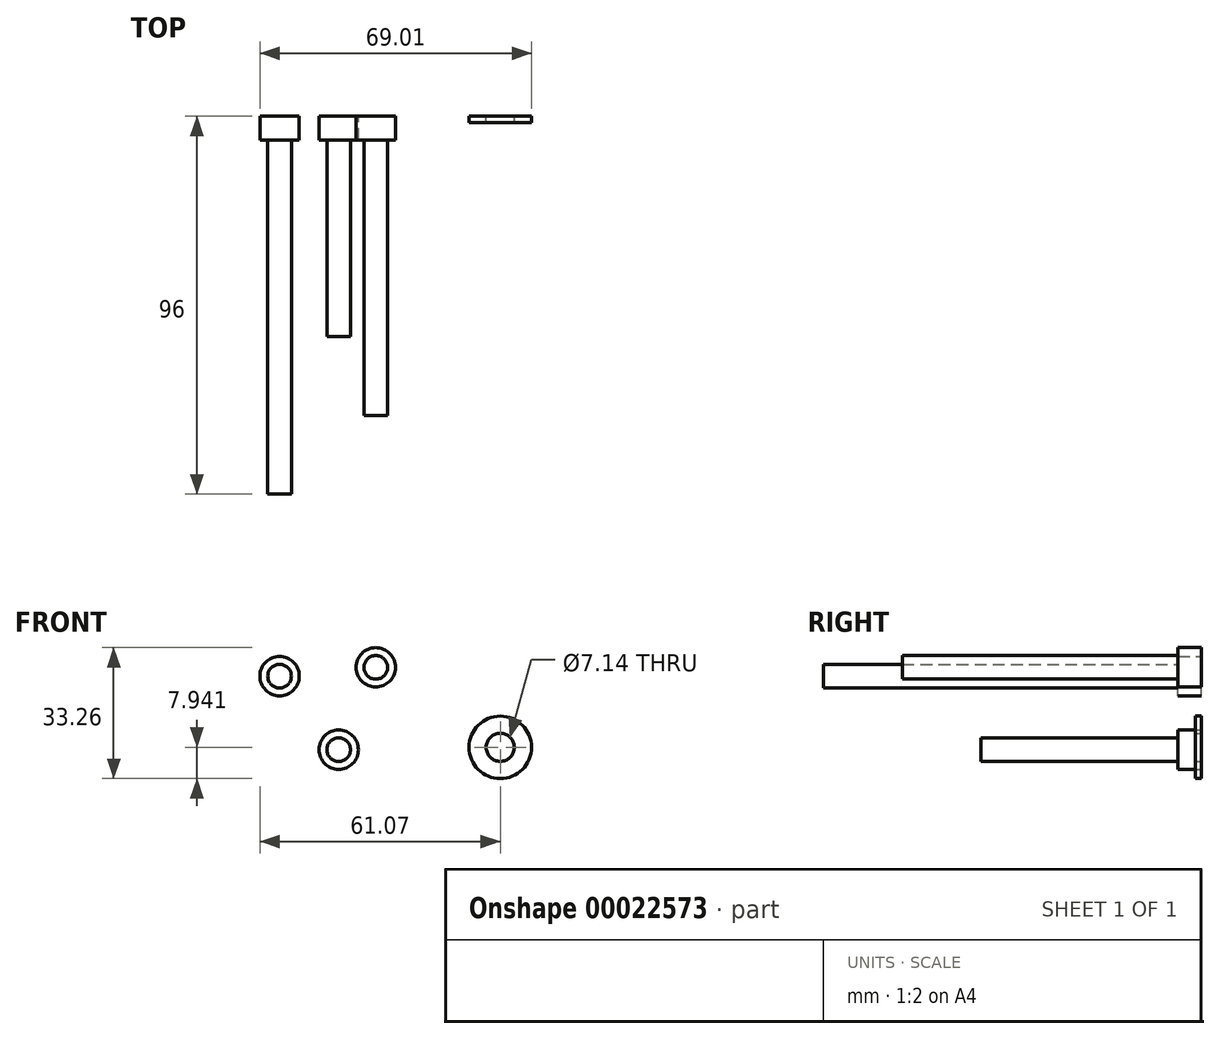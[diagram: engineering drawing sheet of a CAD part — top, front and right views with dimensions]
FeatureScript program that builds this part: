
annotation { "Feature Type Name" : "Feature", "Feature Type Description" : "" }
export const myFeature = defineFeature(function(context is Context, id is Id, definition is map)
    precondition{}
    {
        {
            var Q0;
            Q0=qCreatedBy(makeId("Front.planeOp"),FACE);
            var sketch = newSketch(context, id + "F0", { "sketchPlane" : qUnion([Q0])});
            skCircle(sketch, "E0", {"center": v(-43.19, 35.95) * mm, "radius": 5 * mm});
            skSolve(sketch);
        }
        {
            var Q0;
            Q0=qSketchRegion(id+"F0",true);
            extrude(context, id + "F1", {"entities" : qUnion([Q0]), "depth" : 6 * mm});
        }
        {
            var Q0;
            Q0=makeQuery(id+"F1.opExtrude","CAP_FACE",FACE,{"disambiguationData":[OSD([sQuery(id+"F0.wireOp",EDGE,"E0")])],"isStart":false});
            var sketch = newSketch(context, id + "F2", { "sketchPlane" : qUnion([Q0])});
            skCircle(sketch, "E1", {"center": v(-43.19, 35.95) * mm, "radius": 3 * mm});
            skSolve(sketch);
        }
        {
            var Q0;
            Q0=qSketchRegion(id+"F2",true);
            extrude(context, id + "F3", {"entities" : qUnion([Q0]), "operationType" : NewBodyOperationType.ADD, "depth" : 50 * mm});
        }
        {
            var Q0;
            Q0=qCreatedBy(makeId("Front.planeOp"),FACE);
            var sketch = newSketch(context, id + "F4", { "sketchPlane" : qUnion([Q0])});
            skCircle(sketch, "E2", {"center": v(-2.14, 36.55) * mm, "radius": 3.57 * mm});
            skCircle(sketch, "E3", {"center": v(-2.14, 36.55) * mm, "radius": 7.94 * mm});
            skSolve(sketch);
        }
        {
            var Q0;
            Q0=qSketchRegion(id+"F4",true);
            extrude(context, id + "F5", {"entities" : qUnion([Q0]), "depth" : 1.59 * mm});
        }
        {
            var Q0;
            Q0=qCreatedBy(makeId("Front.planeOp"),FACE);
            var sketch = newSketch(context, id + "F6", { "sketchPlane" : qUnion([Q0])});
            skCircle(sketch, "E4", {"center": v(-33.77, 56.87) * mm, "radius": 5 * mm});
            skSolve(sketch);
        }
        {
            var Q0;
            Q0=qSketchRegion(id+"F6",true);
            extrude(context, id + "F7", {"entities" : qUnion([Q0]), "depth" : 6 * mm});
        }
        {
            var Q0;
            Q0=makeQuery(id+"F7.opExtrude","CAP_FACE",FACE,{"disambiguationData":[OSD([sQuery(id+"F6.wireOp",EDGE,"E4")])],"isStart":false});
            var sketch = newSketch(context, id + "F8", { "sketchPlane" : qUnion([Q0])});
            skCircle(sketch, "E5", {"center": v(-33.77, 56.87) * mm, "radius": 3 * mm});
            skSolve(sketch);
        }
        {
            var Q0;
            Q0=qSketchRegion(id+"F8",true);
            extrude(context, id + "F9", {"entities" : qUnion([Q0]), "operationType" : NewBodyOperationType.ADD, "depth" : 70 * mm});
        }
        {
            var Q0;
            Q0=qCreatedBy(makeId("Front.planeOp"),FACE);
            var sketch = newSketch(context, id + "F10", { "sketchPlane" : qUnion([Q0])});
            skCircle(sketch, "E6", {"center": v(-58.2, 54.64) * mm, "radius": 5 * mm});
            skSolve(sketch);
        }
        {
            var Q0;
            Q0=qSketchRegion(id+"F10",true);
            extrude(context, id + "F11", {"entities" : qUnion([Q0]), "depth" : 6 * mm});
        }
        {
            var Q0;
            Q0=makeQuery(id+"F11.opExtrude","CAP_FACE",FACE,{"disambiguationData":[OSD([sQuery(id+"F10.wireOp",EDGE,"E6")])],"isStart":false});
            var sketch = newSketch(context, id + "F12", { "sketchPlane" : qUnion([Q0])});
            skCircle(sketch, "E7", {"center": v(-58.2, 54.64) * mm, "radius": 3 * mm});
            skSolve(sketch);
        }
        {
            var Q0;
            Q0=qSketchRegion(id+"F12",true);
            extrude(context, id + "F13", {"entities" : qUnion([Q0]), "operationType" : NewBodyOperationType.ADD, "depth" : 90 * mm});
        }
    });
